# Revit family: Intersan Sanifount
name_source: partatom
category: Plumbing Fixtures
revit_build: Autodesk Revit 2017 (Build: 20170816_0615(x64)
units: mm (PartAtom-declared; Revit-internal decimal feet)

## family parameters
Always vertical = Yes
Cut with Voids When Loaded = No
OmniClass Number = 23.45.05.14.14
OmniClass Title = Sinks/Lavatories
Part Type = Normal
Room Calculation Point = No
Round Connector Dimension = Use Diameter
Shared = No
Work Plane-Based = No

## types (2) — shared parameters
CW Connection = Yes
Drain Diameter = 1 1/2"
HW Connection = Yes
Manufacturer = Intersan
Material = Anti-microbial Solid Surface and Stainless Steel
Model = Sanifount
Supply Cold Diameter = 1/2"
Supply Hot Diameter = 1/2"
Warranty = 5 years on material - 3 years on components
Waste Connection = Yes
Water Usage = 0.5 gpm/user

## per-type parameters (varying)
| type | Unit Depth | Unit Height | Unit Width |
| 3-user | 25 1/4" | 20 1/4" | 35 1/2" |
| 4-user | 25 1/2" | 20 3/8" | 48" |

## geometry (parser evidence)
native form markers: Sweep x3
no freeform markers — native parametric forms only
